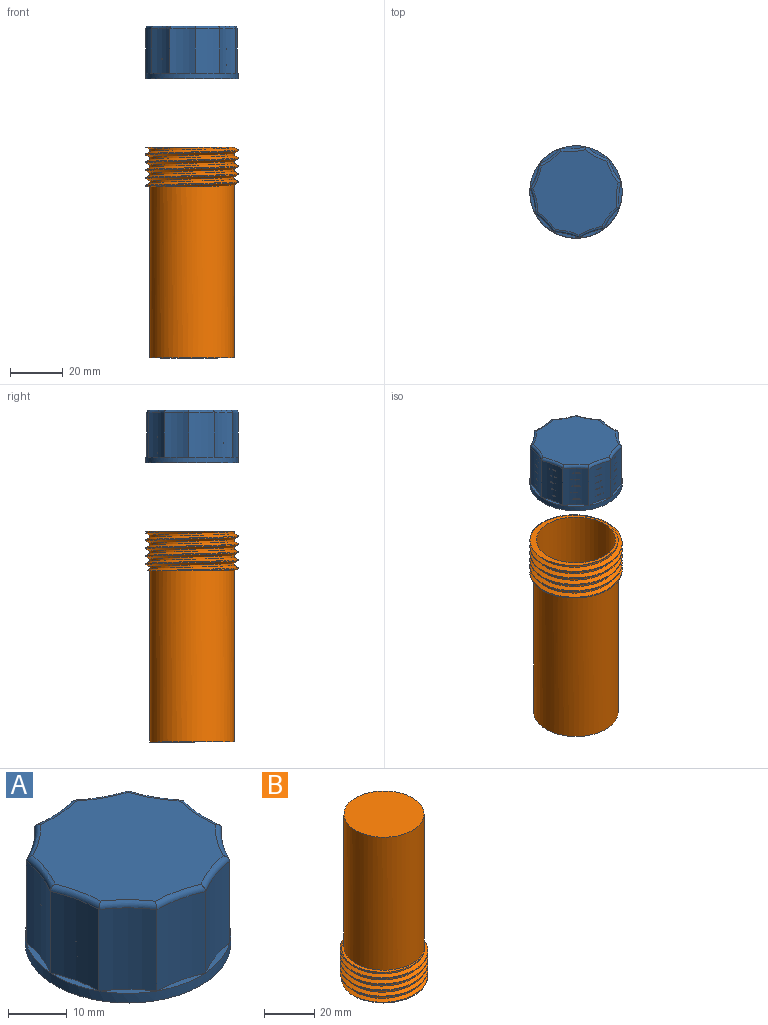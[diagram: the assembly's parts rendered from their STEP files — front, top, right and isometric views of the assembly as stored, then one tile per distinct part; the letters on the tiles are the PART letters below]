
ASSEMBLY  parts=2 mates=1
PART A: 44 faces, bbox 35.9x38.5x22 mm
  f0: plane 31.29x31.28mm, normal (0,0,-1), area 728.8mm2, adj f40,f41,f42,f43
  f1: cylinder r=24.56mm len=17mm, axis (0,0,1), area 168.8mm2, adj f2,f11,f13,f32
  f2: cylinder r=24.56mm len=17mm, axis (0,0,1), area 168.8mm2, adj f1,f3,f23,f30
  f3: cylinder r=24.56mm len=17mm, axis (0,0,1), area 168.8mm2, adj f2,f4,f22,f28
  f4: cylinder r=24.56mm len=17mm, axis (0,0,1), area 168.8mm2, adj f3,f5,f21,f26
  f5: cylinder r=24.56mm len=17mm, axis (0,0,1), area 168.8mm2, adj f4,f6,f20,f27
  f6: cylinder r=24.56mm len=17mm, axis (0,0,1), area 168.8mm2, adj f5,f7,f19,f29
  f7: cylinder r=24.56mm len=17mm, axis (0,0,1), area 168.8mm2, adj f6,f8,f18,f31
  f8: cylinder r=24.56mm len=17mm, axis (0,0,1), area 168.8mm2, adj f7,f9,f17,f33
  f9: cylinder r=24.56mm len=17mm, axis (0,0,1), area 168.8mm2, adj f8,f10,f16,f35
  f10: cylinder r=24.56mm len=17mm, axis (0,0,1), area 168.8mm2, adj f9,f11,f15,f36
  f11: cylinder r=24.56mm len=17mm, axis (0,0,1), area 168.8mm2, adj f1,f10,f14,f34
  f12: plane 32.34x32.33mm, normal (0,0,1), area 768.8mm2, adj f26,f27,f28,f29,f30,f31,f32,f33
  f13: plane 9.83x1.32mm, normal (0,0,1), area 8mm2, adj f1,f25
  f14: plane 7.89x5.92mm, normal (0,0,1), area 8mm2, adj f11,f25
  f15: plane 9.24x3.43mm, normal (0,0,1), area 8mm2, adj f10,f25
  f16: plane 9.63x2.15mm, normal (0,0,1), area 8mm2, adj f9,f25
  f17: plane 6.98x6.96mm, normal (0,0,1), area 8mm2, adj f8,f25
  f18: plane 9.64x2.13mm, normal (0,0,1), area 8mm2, adj f7,f25
  f19: plane 9.23x3.46mm, normal (0,0,1), area 8mm2, adj f6,f25
  f20: plane 7.9x5.9mm, normal (0,0,1), area 8mm2, adj f5,f25
  f21: plane 9.84x1.31mm, normal (0,0,1), area 8mm2, adj f4,f25
  f22: plane 8.65x4.74mm, normal (0,0,1), area 8mm2, adj f3,f25
  f23: plane 8.66x4.71mm, normal (0,0,1), area 8mm2, adj f2,f25
  f24: plane 35.73x35.73mm, normal (0,0,-1), area 243.1mm2, adj f25,f37,f38,f39,f43
  f25: cylinder r=17.5mm len=35mm, axis (0,0,1), area 219.9mm2, adj f13,f14,f15,f16,f17,f18,f19,f20
  f26: torus R=25.56mm, axis (0,0,1), area 15mm2, adj f4,f12,f27,f28
  f27: torus R=25.56mm, axis (0,0,1), area 15mm2, adj f5,f12,f26,f29
  f28: torus R=25.56mm, axis (0,0,1), area 15mm2, adj f3,f12,f26,f30
  f29: torus R=25.56mm, axis (0,0,1), area 15mm2, adj f6,f12,f27,f31
  f30: torus R=25.56mm, axis (0,0,1), area 15mm2, adj f2,f12,f28,f32
  f31: torus R=25.56mm, axis (0,0,1), area 15mm2, adj f7,f12,f29,f33
  f32: torus R=25.56mm, axis (0,0,1), area 15mm2, adj f1,f12,f30,f34
  f33: torus R=25.56mm, axis (0,0,1), area 15mm2, adj f8,f12,f31,f35
  f34: torus R=25.56mm, axis (0,0,1), area 15mm2, adj f11,f12,f32,f36
  f35: torus R=25.56mm, axis (0,0,1), area 15mm2, adj f9,f12,f33,f36
  f36: torus R=25.56mm, axis (0,0,1), area 15mm2, adj f10,f12,f34,f35
  f37: bspline ~32.55x32.39mm, area 95.4mm2, adj f24,f39,f41,f43
  f38: bspline ~26.04x16.39mm, area 28.6mm2, adj f24,f39,f40
  f39: bspline ~32.66x22.26mm, area 16.5mm2, adj f24,f37,f38,f42
  f40: bspline ~37.24x32.25mm, area 1054.4mm2, adj f0,f38,f42,f43
  f41: bspline ~37.24x32.25mm, area 975.8mm2, adj f0,f37,f42,f43
  f42: bspline ~37.55x32.52mm, area 248.7mm2, adj f0,f39,f40,f41
  f43: cylinder r=14.5mm len=29mm, axis (0,0,1), area 429.3mm2, adj f0,f24,f37,f40,f41
PART B: 14 faces, bbox 35.8x35.8x83.9 mm
  f0: cylinder r=16mm len=65.89mm, axis (0,0,1), area 6547.9mm2, adj f1,f7,f11,f12
  f1: cylinder r=16mm len=32mm, axis (0,0,1), area 89.8mm2, adj f0,f2,f12,f13
  f2: cylinder r=16mm len=32mm, axis (0,0,1), area 89.8mm2, adj f1,f3,f12,f13
  f3: cylinder r=16mm len=32mm, axis (0,0,1), area 89.8mm2, adj f2,f4,f12,f13
  f4: cylinder r=16mm len=32mm, axis (0,0,1), area 89.8mm2, adj f3,f5,f12,f13
  f5: cylinder r=16mm len=32mm, axis (0,0,1), area 76.5mm2, adj f4,f6,f12,f13
  f6: plane 34.27x33.87mm, normal (0,0,-1), area 162.1mm2, adj f5,f8,f10,f12,f13
  f7: plane 32x32mm, normal (0,0,1), area 804.2mm2, adj f0
  f8: cylinder r=15mm len=79mm, axis (0,0,1), area 7445.6mm2, adj f6,f9
  f9: plane 30x30mm, normal (0,0,-1), area 706.9mm2, adj f8
  f10: cylinder r=17.5mm len=35mm, axis (0,0,-1), area 210.1mm2, adj f6,f11,f12,f13
  f11: plane 33.87x31.99mm, normal (0,0,1), area 64.7mm2, adj f0,f10,f12,f13
  f12: bspline ~34.97x34.93mm, area 1735.6mm2, adj f0,f1,f2,f3,f4,f5,f6,f10
  f13: bspline ~34.97x34.97mm, area 2061.5mm2, adj f1,f2,f3,f4,f5,f6,f10,f11
PLACE A t=(0,-16.5,-106.33)mm
PLACE B rot(axis=(1,0,0),180deg) t=(0,-16.5,-272.22)mm
MATE slider B.f0 <-> A.f25  axis (0,0,-1) through (0,-16.5,-152.22)mm
